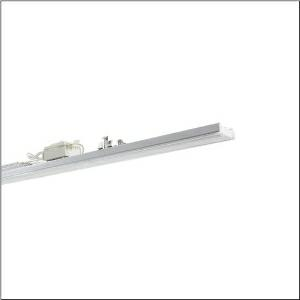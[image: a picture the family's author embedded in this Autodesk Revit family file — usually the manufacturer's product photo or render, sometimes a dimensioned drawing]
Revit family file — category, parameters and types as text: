
# Revit family: licross_21_recessed_ho_52te12dv4l2m3s
name_source: partatom
category: Lighting Fixtures
units: mm (PartAtom-declared; Revit-internal decimal feet)

## family parameters
Cut with Voids When Loaded = No
Host = Face
Light Source = No
Part Type = Normal
Room Calculation Point = No
Round Connector Dimension = Use Diameter
Shared = No

## types (1)
- --- (1 x LED, 910 lm, 6.4 W, 4000K)
    Apparent Load = 6 VA
    CIE Flux Codes = 69 91 98 100 100
    Color Rendering = 80
    Color Temperature = 4000K
    Default Elevation = 1800 mm
    Description = Licross 21 Recessed HO, luminaire insert, of sheet steel, galvanised, coil coated, white, length: 2.250mm, width: 66mm, height: 67mm, LED rated luminous flux: 22.710lm, light colour: 840, SDCM (Standard Deviation of Colour Matching)MacAdam ≤ 3 SDCM (initial), control gear: DALI 2 (for two DALI lines), with plug, 6-pole, with phase selection, for trunking rail, 14-core, mains connection: 220..240V, AC, 50/60Hz, rated input power: 129W, for trunking rail, 14-core, internal wiring halogen-free, for emergency light function, converter,control gear: single battery element, battery: LiFePO4, 9Ah, primary optical cover: cover, of PMMA, light emission: direct distribution, primary light characteristic: symmetric, protection rating (complete): IP54, insulation class (complete): insulation class I (protective earthing), certification: CE, UKCA, protection symbol: D if used in an environment with non-conductive dust loads with corresponding accessories, impact resistance: IK06, permissible ambient temperature for indoor applications: +5..+30°C, standard: EN 60598-2-22, LABS conformity tested according to VDMA 24364:2018-05, reducing of maximum allowable ambient temperature of 5°C with ceiling mounting, corresponds to IFS (International Featured Standards) requirements for safety and quality in the food industry, The light source and the operating device comply with the requirements of the Ecodesign Regulation (EU) 2019/2020 and are replaceable in accordance with this regulation, packaging unit: 1 piece
    Height = 58 mm
    Lamp = 1 x LED
    Lamp Light Flux = 910 lm
    Lamp Power = 6.4 W
    Lamp count = 1
    Length = 2250 mm
    Luminous efficacy = 142 lm/W
    Manufacturer = Siteco
    ModVariant = No
    Model = 52TE12DV4L2M3S
    Mounting Place = Ceiling
    Mounting Type = Pendant
    Number of Poles = 1
    OnlyDefault = Yes
    Power Factor = 1
    Product Name = Licross 21 Recessed HO
    Product group = luminaire insert | ceiling pendant
    ProductGroupID = 901
    Protection Class = Protection class I
    Protection Degree = IP 54
    RLX_Detail_Level = 1
    RLX_Emergency_Light_Flux = 0 lm
    RLX_Emergency_Type = 0
    RLX_Emergency_Type_DB = No
    RlxData = <blob elided: 30273 chars, md5=94702196>
    Socket = socket
    Standby Power = 0 W
    System Light Flux = 910 lm
    System Power = 6 W
    Type Comments = : emergency light operation: 3 h
    Type Image = l_1296930.jpg
    URL = http://relux.com
    VarID = @adj_109237
    Voltage = 0 V
    Weight = 0.00 kg
    Width = 66 mm

## geometry (parser evidence)
native form markers: Blend x4, Sweep x10
no freeform markers — native parametric forms only
